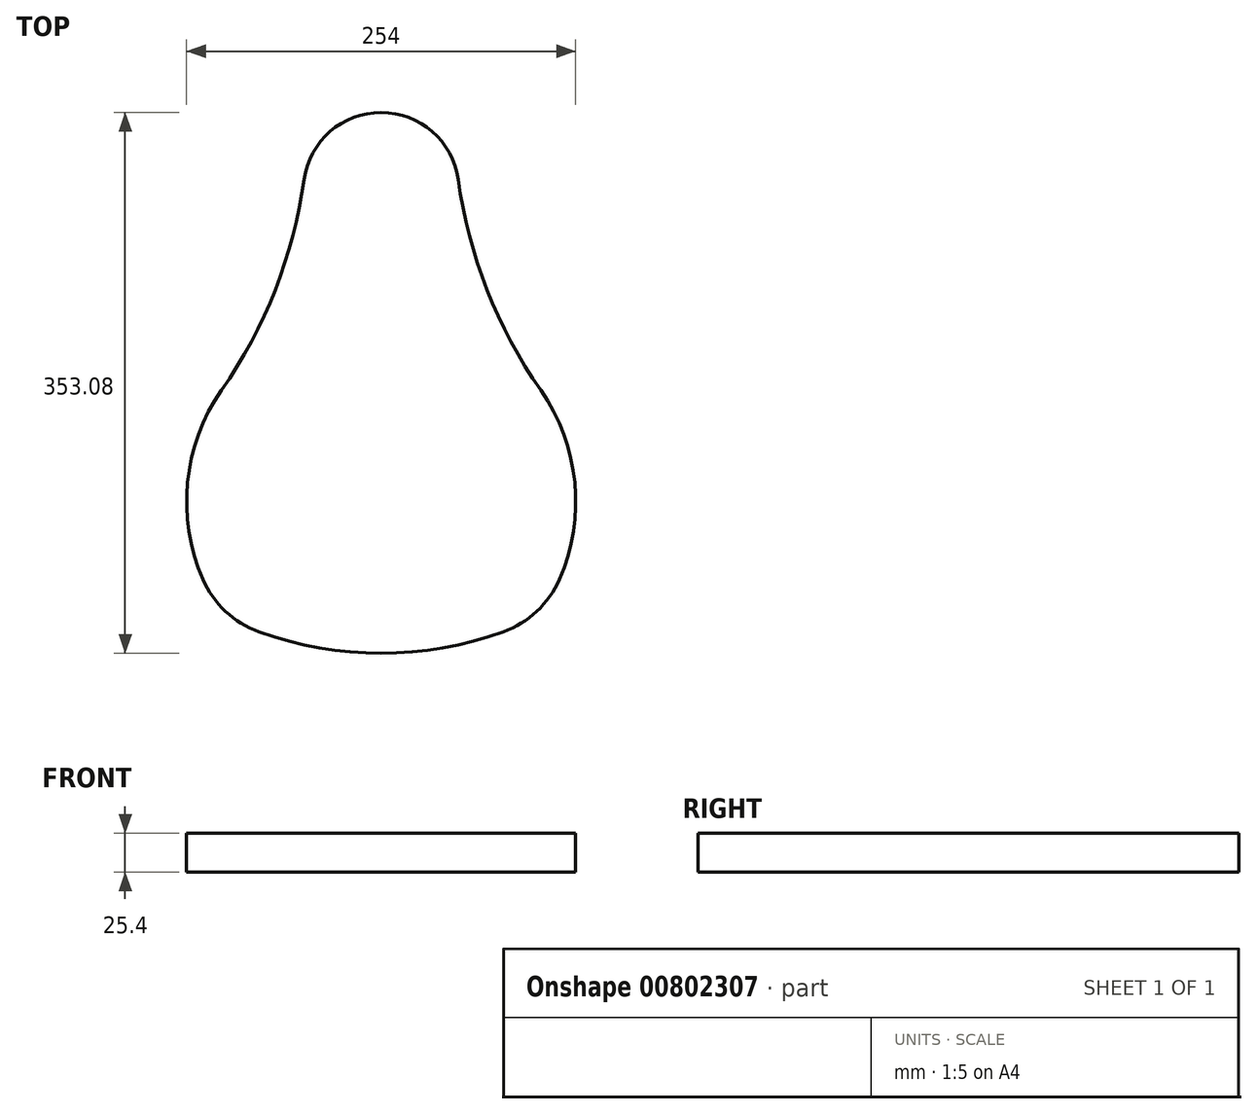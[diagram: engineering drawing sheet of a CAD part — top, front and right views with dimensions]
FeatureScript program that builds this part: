
annotation { "Feature Type Name" : "Feature", "Feature Type Description" : "" }
export const myFeature = defineFeature(function(context is Context, id is Id, definition is map)
    precondition{}
    {
        {
            var Q0;
            Q0=qCreatedBy(makeId("Top.planeOp"),FACE);
            var sketch = newSketch(context, id + "F0", { "sketchPlane" : qUnion([Q0])});
            skCircle(sketch, "E0", {"center": v(0, 0) * mm, "radius": 127 * mm});
            skCircle(sketch, "E1", {"center": v(0, 203.2) * mm, "radius": 50.8 * mm});
            skArc(sketch, "E2", {"start": v(50.31, 210.2) * mm, "mid": v(69.15, 138.2) * mm, "end": v(104.22, 72.57) * mm});
            skArc(sketch, "E3", {"start": v(-104.22, 72.57) * mm, "mid": v(-69.15, 138.2) * mm, "end": v(-50.31, 210.2) * mm});
            skCircle(sketch, "E4", {"center": v(-58.2, -25.4) * mm, "radius": 63.5 * mm});
            skCircle(sketch, "E5", {"center": v(58.2, -25.4) * mm, "radius": 63.5 * mm});
            skArc(sketch, "E6", {"start": v(-79.75, -85.13) * mm, "mid": v(0, -99.08) * mm, "end": v(79.75, -85.13) * mm});
            skSolve(sketch);
        }
        {
            var Q0;
            {var subQ1=sQuery(id+"F0.wireOp",EDGE,"E0");var subQ5=makeQuery(id+"F0.imprint","INTERSECT",VERTEX,{"derivedFrom":[subQ1,sQuery(id+"F0.wireOp",EDGE,"E2")]});Q0=makeQuery(id+"F0.imprint","IMPRINT",FACE,{"disambiguationData":[TD([[makeQuery(id+"F0.imprint","IMPRINT",EDGE,{"disambiguationData":[TD([[subQ5,-1.0]])],"derivedFrom":subQ1}),1.0]])]});}
            var Q1;
            {var subQ0=sQuery(id+"F0.wireOp",EDGE,"E4");var subQ1=makeQuery(id+"F0.imprint","INTERSECT",VERTEX,{"derivedFrom":[sQuery(id+"F0.wireOp",EDGE,"E0"),subQ0]});Q1=makeQuery(id+"F0.imprint","IMPRINT",FACE,{"disambiguationData":[TD([[makeQuery(id+"F0.imprint","IMPRINT",EDGE,{"disambiguationData":[TD([[subQ1,1.0]])],"derivedFrom":subQ0}),1.0]])]});}
            var Q2;
            {var subQ0=sQuery(id+"F0.wireOp",EDGE,"E5");var subQ1=sQuery(id+"F0.wireOp",EDGE,"E4");var subQ2=makeQuery(id+"F0.imprint","INTERSECT",VERTEX,{"disambiguationData":[OD(0.0)],"derivedFrom":[subQ1,subQ0]});Q2=makeQuery(id+"F0.imprint","IMPRINT",FACE,{"disambiguationData":[TD([[makeQuery(id+"F0.imprint","IMPRINT",EDGE,{"disambiguationData":[TD([[subQ2,1.0]])],"derivedFrom":subQ1}),1.0]])]});}
            var Q3;
            {var subQ0=sQuery(id+"F0.wireOp",EDGE,"E5");var subQ1=sQuery(id+"F0.wireOp",EDGE,"E4");var subQ2=makeQuery(id+"F0.imprint","INTERSECT",VERTEX,{"disambiguationData":[OD(0.0)],"derivedFrom":[subQ1,subQ0]});Q3=makeQuery(id+"F0.imprint","IMPRINT",FACE,{"disambiguationData":[TD([[makeQuery(id+"F0.imprint","IMPRINT",EDGE,{"disambiguationData":[TD([[subQ2,1.0]])],"derivedFrom":subQ1}),-1.0]])]});}
            var Q4;
            {var subQ0=sQuery(id+"F0.wireOp",EDGE,"E6");Q4=makeQuery(id+"F0.imprint","IMPRINT",FACE,{"disambiguationData":[TD([[makeQuery(id+"F0.imprint","IMPRINT",EDGE,{"derivedFrom":subQ0}),1.0]])]});}
            var Q5;
            {var subQ0=sQuery(id+"F0.wireOp",EDGE,"E2");Q5=makeQuery(id+"F0.imprint","IMPRINT",FACE,{"disambiguationData":[TD([[makeQuery(id+"F0.imprint","IMPRINT",EDGE,{"derivedFrom":subQ0}),-1.0]])]});}
            var Q6;
            {var subQ0=sQuery(id+"F0.wireOp",EDGE,"E1");var subQ1=makeQuery(id+"F0.imprint","INTERSECT",VERTEX,{"derivedFrom":[subQ0,sQuery(id+"F0.wireOp",EDGE,"E2")]});Q6=makeQuery(id+"F0.imprint","IMPRINT",FACE,{"disambiguationData":[TD([[makeQuery(id+"F0.imprint","IMPRINT",EDGE,{"disambiguationData":[TD([[subQ1,-1.0]])],"derivedFrom":subQ0}),1.0]])]});}
            extrude(context, id + "F1", {"entities" : qUnion([Q0, Q1, Q2, Q3, Q4, Q5, Q6]), "depth" : 25.4 * mm, "offsetDistance" : 25.4 * mm});
        }
    });
